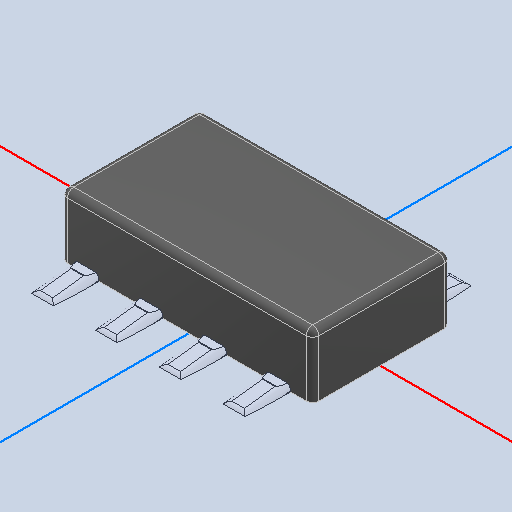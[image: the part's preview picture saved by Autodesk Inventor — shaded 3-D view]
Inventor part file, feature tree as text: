
AUTODESK INVENTOR PART (.ipt)
format: ipt  version: 2022 (Build 260153000, 153)  size: 171,520 bytes
history: native  units: mm
features: other x12, mirror x4, fillet x2
ambient origin geometry x8: Origin, YZ Plane, XZ Plane, XY Plane, X Axis, Y Axis, Z Axis, Center Point
bodies: Body1 (feature_tree), Body2 (feature_tree), Body3 (feature_tree), Body4 (feature_tree), Body5 (feature_tree), Body6 (feature_tree), Body7 (feature_tree), Body8 (feature_tree), Body9 (feature_tree)
feature tree (18):
  other  "Твердое тело1"
  other  "Твердое тело2"
  other  "Твердое тело3"
  other  "Твердое тело4"
  other  "Твердое тело5"
  other  "Твердое тело6"
  other  "Твердое тело7"
  other  "Твердое тело8"
  other  "Твердое тело9"
  fillet  "Fillet2"  [1 undecoded]
  fillet  "Fillet1"  [1 undecoded]
  other  "LPattern3[1]"
  other  "LPattern3[2]"
  other  "LPattern3[3]"
  mirror  "Mirror1[1]"
  mirror  "Mirror1[2]"
  mirror  "Mirror1[3]"
  mirror  "Mirror1[4]"
note: 2 required parameter values undecoded (feature->parameter linkage not recoverable at this tier; creation-order binding heuristic only, values carry confidence <= 0.55)
